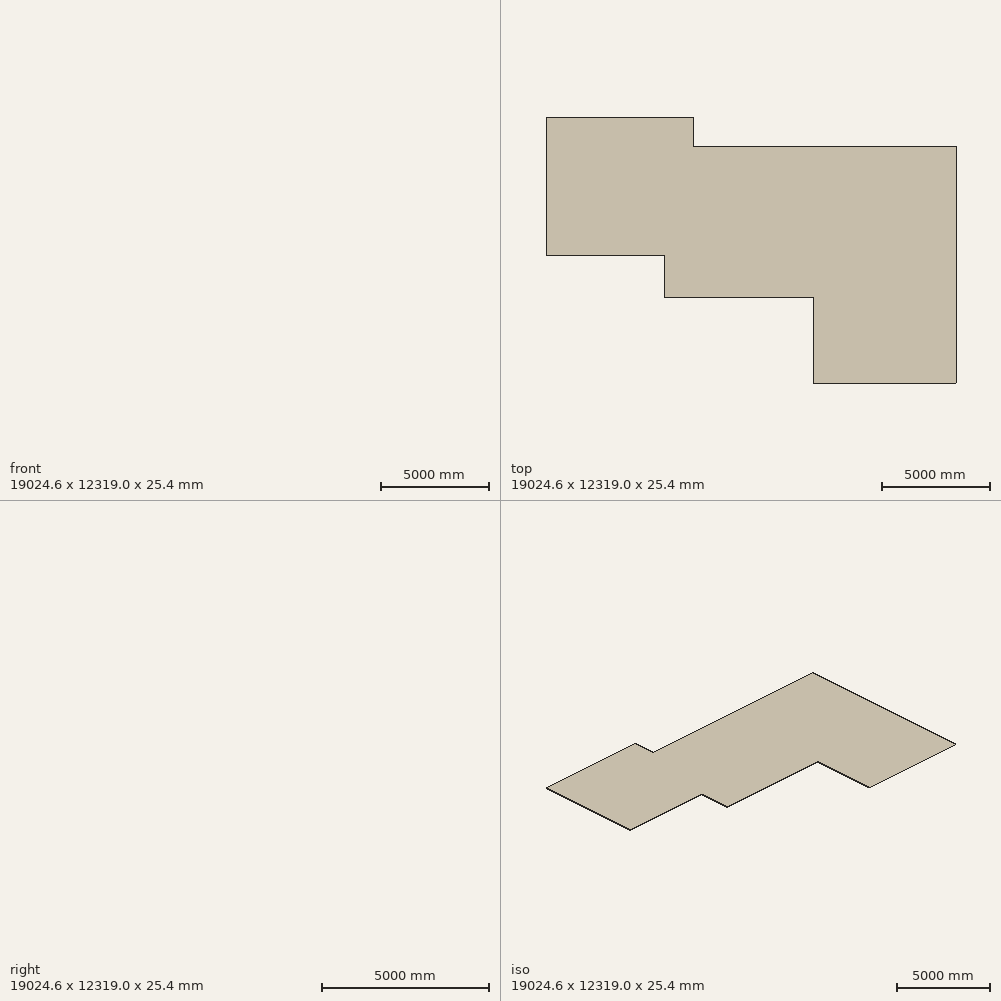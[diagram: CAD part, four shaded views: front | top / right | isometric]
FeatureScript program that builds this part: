
annotation { "Feature Type Name" : "Feature", "Feature Type Description" : "" }
export const myFeature = defineFeature(function(context is Context, id is Id, definition is map)
    precondition{}
    {
        {
            var Q0;
            Q0=qCreatedBy(makeId("Top.planeOp"),FACE);
            var sketch = newSketch(context, id + "F0", { "sketchPlane" : qUnion([Q0])});
            skLineSegment(sketch, "E0", {"start": v(0, 0) * mm, "end": v(0, 6400.8) * mm});
            skLineSegment(sketch, "E1", {"start": v(0, 6400.8) * mm, "end": v(6832.6, 6400.8) * mm});
            skLineSegment(sketch, "E2", {"start": v(6832.6, 6400.8) * mm, "end": v(6832.6, 5054.6) * mm});
            skLineSegment(sketch, "E3", {"start": v(6832.6, 5054.6) * mm, "end": v(19024.6, 5054.6) * mm});
            skLineSegment(sketch, "E4", {"start": v(19024.6, 5054.6) * mm, "end": v(19024.6, -5918.2) * mm});
            skLineSegment(sketch, "E5", {"start": v(19024.6, -5918.2) * mm, "end": v(12395.2, -5918.2) * mm});
            skLineSegment(sketch, "E6", {"start": v(12395.2, -5918.2) * mm, "end": v(12395.2, -1955.8) * mm});
            skLineSegment(sketch, "E7", {"start": v(12395.2, -1955.8) * mm, "end": v(5486.4, -1955.8) * mm});
            skLineSegment(sketch, "E8", {"start": v(5486.4, -1955.8) * mm, "end": v(5486.4, 0) * mm});
            skLineSegment(sketch, "E9", {"start": v(5486.4, 0) * mm, "end": v(0, 0) * mm});
            skSolve(sketch);
        }
        {
            var Q0;
            Q0=makeQuery(id+"F0.imprint","IMPRINT",FACE,{"disambiguationData":[TD([[makeQuery(id+"F0.imprint","IMPRINT",EDGE,{"derivedFrom":sQuery(id+"F0.wireOp",EDGE,"E0")}),-1.0]])]});
            extrude(context, id + "F1", {"entities" : qUnion([Q0]), "depth" : 25.4 * mm, "offsetDistance" : 25.4 * mm});
        }
    });
